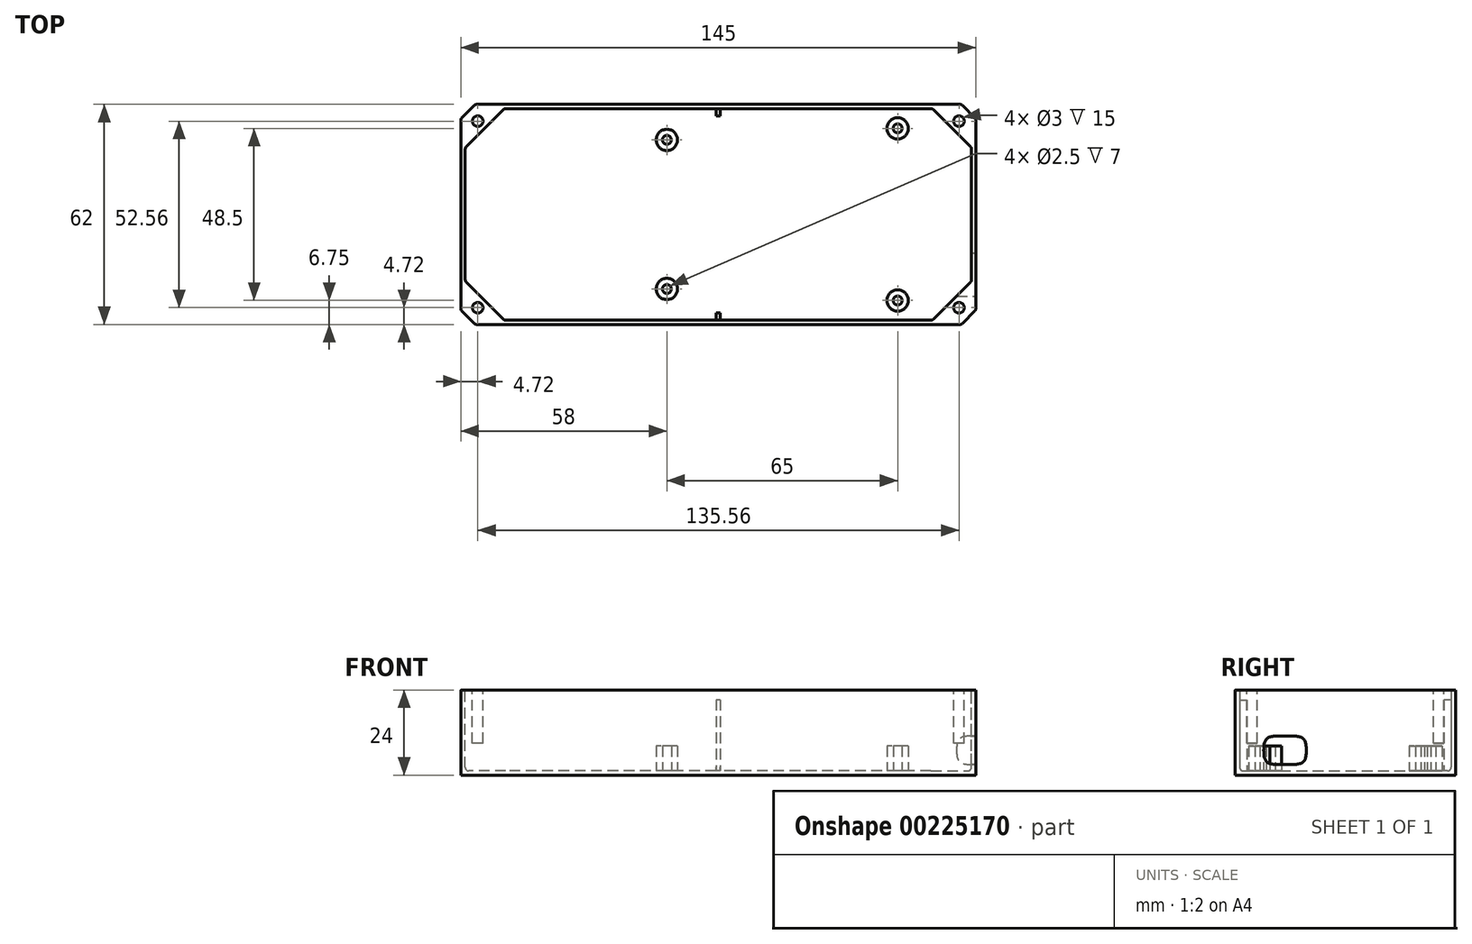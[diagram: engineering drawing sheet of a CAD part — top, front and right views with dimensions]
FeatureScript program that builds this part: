
annotation { "Feature Type Name" : "Feature", "Feature Type Description" : "" }
export const myFeature = defineFeature(function(context is Context, id is Id, definition is map)
    precondition{}
    {
        {
            var Q0;
            Q0=qCreatedBy(makeId("Top.planeOp"),FACE);
            var sketch = newSketch(context, id + "F0", { "sketchPlane" : qUnion([Q0])});
            skLineSegment(sketch, "E0.bottom", {"start": v(72.5, -31) * mm, "end": v(-72.5, -31) * mm});
            skLineSegment(sketch, "E0.top", {"start": v(72.5, 31) * mm, "end": v(-72.5, 31) * mm});
            skLineSegment(sketch, "E0.left", {"start": v(72.5, -31) * mm, "end": v(72.5, 31) * mm});
            skLineSegment(sketch, "E0.right", {"start": v(-72.5, -31) * mm, "end": v(-72.5, 31) * mm});
            skPoint(sketch, "E0.middle", {"position": v(0, 0) * mm});
            skSolve(sketch);
        }
        {
            var Q0;
            Q0=qSketchRegion(id+"F0",true);
            extrude(context, id + "F1", {"entities" : qUnion([Q0]), "depth" : 24 * mm});
        }
        {
            var Q0;
            Q0=makeQuery(id+"F1.opExtrude","CAP_FACE",FACE,{"disambiguationData":[OSD([sQuery(id+"F0.wireOp",EDGE,"E0.bottom"),sQuery(id+"F0.wireOp",EDGE,"E0.top"),sQuery(id+"F0.wireOp",EDGE,"E0.left"),sQuery(id+"F0.wireOp",EDGE,"E0.right")])],"isStart":false});
            var Q1;
            Q1=makeQuery(id+"F1.opExtrude","SWEPT_BODY",BODY,{"disambiguationData":[OSD([sQuery(id+"F0.wireOp",EDGE,"E0.bottom"),sQuery(id+"F0.wireOp",EDGE,"E0.top"),sQuery(id+"F0.wireOp",EDGE,"E0.left"),sQuery(id+"F0.wireOp",EDGE,"E0.right")])]});
            shell(context, id + "F2", {"entities" : qUnion([Q0]), "parts" : qUnion([Q1]), "thickness" : 1.2 * mm});
        }
        {
            var Q0;
            Q0=makeQuery(id+"F2.opShell","OFFSET_EDGE",EDGE,{"disambiguationData":[OSD([sQuery(id+"F0.wireOp",EDGE,"E0.top"),sQuery(id+"F0.wireOp",EDGE,"E0.left")])]});
            var Q1;
            Q1=makeQuery(id+"F2.opShell","OFFSET_EDGE",EDGE,{"disambiguationData":[OSD([sQuery(id+"F0.wireOp",EDGE,"E0.top"),sQuery(id+"F0.wireOp",EDGE,"E0.right")])]});
            var Q2;
            Q2=makeQuery(id+"F2.opShell","OFFSET_EDGE",EDGE,{"disambiguationData":[OSD([sQuery(id+"F0.wireOp",EDGE,"E0.bottom"),sQuery(id+"F0.wireOp",EDGE,"E0.right")])]});
            var Q3;
            Q3=makeQuery(id+"F2.opShell","OFFSET_EDGE",EDGE,{"disambiguationData":[OSD([sQuery(id+"F0.wireOp",EDGE,"E0.bottom"),sQuery(id+"F0.wireOp",EDGE,"E0.left")])]});
            chamfer(context, id + "F3", {"entities" : qUnion([Q0, Q1, Q2, Q3]), "width" : 11 * mm, "tangentPropagation" : true});
        }
        {
            var Q0;
            Q0=makeQuery(id+"F1.opExtrude","SWEPT_EDGE",EDGE,{"disambiguationData":[OSD([sQuery(id+"F0.wireOp",EDGE,"E0.bottom"),sQuery(id+"F0.wireOp",EDGE,"E0.right")])]});
            var Q1;
            Q1=makeQuery(id+"F1.opExtrude","SWEPT_EDGE",EDGE,{"disambiguationData":[OSD([sQuery(id+"F0.wireOp",EDGE,"E0.top"),sQuery(id+"F0.wireOp",EDGE,"E0.right")])]});
            var Q2;
            Q2=makeQuery(id+"F1.opExtrude","SWEPT_EDGE",EDGE,{"disambiguationData":[OSD([sQuery(id+"F0.wireOp",EDGE,"E0.bottom"),sQuery(id+"F0.wireOp",EDGE,"E0.left")])]});
            var Q3;
            Q3=makeQuery(id+"F1.opExtrude","SWEPT_EDGE",EDGE,{"disambiguationData":[OSD([sQuery(id+"F0.wireOp",EDGE,"E0.top"),sQuery(id+"F0.wireOp",EDGE,"E0.left")])]});
            chamfer(context, id + "F4", {"entities" : qUnion([Q0, Q1, Q2, Q3]), "width" : 4 * mm, "tangentPropagation" : true});
        }
        {
            var Q0;
            Q0=makeQuery(id+"F1.opExtrude","CAP_FACE",FACE,{"disambiguationData":[OSD([sQuery(id+"F0.wireOp",EDGE,"E0.bottom"),sQuery(id+"F0.wireOp",EDGE,"E0.top"),sQuery(id+"F0.wireOp",EDGE,"E0.left"),sQuery(id+"F0.wireOp",EDGE,"E0.right")])],"isStart":false});
            var sketch = newSketch(context, id + "F5", { "sketchPlane" : qUnion([Q0])});
            skCircle(sketch, "E1", {"center": v(-67.78, -26.28) * mm, "radius": 1.5 * mm});
            skCircle(sketch, "E2", {"center": v(-67.78, 26.28) * mm, "radius": 1.5 * mm});
            skCircle(sketch, "E3", {"center": v(67.78, 26.28) * mm, "radius": 1.5 * mm});
            skCircle(sketch, "E4", {"center": v(67.78, -26.28) * mm, "radius": 1.5 * mm});
            skLineSegment(sketch, "E5", {"start": v(-70.5, -29) * mm, "end": v(-65.8, -24.3) * mm, "construction": true});
            skLineSegment(sketch, "E6", {"start": v(-70.5, 29) * mm, "end": v(-65.8, 24.3) * mm, "construction": true});
            skLineSegment(sketch, "E7", {"start": v(70.5, 29) * mm, "end": v(65.8, 24.3) * mm, "construction": true});
            skLineSegment(sketch, "E8", {"start": v(70.5, -29) * mm, "end": v(65.8, -24.3) * mm, "construction": true});
            skSolve(sketch);
        }
        {
            var Q0;
            Q0=makeQuery(id+"F5.imprint","IMPRINT",FACE,{"disambiguationData":[TD([[makeQuery(id+"F5.imprint","IMPRINT",EDGE,{"derivedFrom":sQuery(id+"F5.wireOp",EDGE,"E2")}),1.0]])]});
            var Q1;
            Q1=makeQuery(id+"F5.imprint","IMPRINT",FACE,{"disambiguationData":[TD([[makeQuery(id+"F5.imprint","IMPRINT",EDGE,{"derivedFrom":sQuery(id+"F5.wireOp",EDGE,"E1")}),1.0]])]});
            var Q2;
            Q2=makeQuery(id+"F5.imprint","IMPRINT",FACE,{"disambiguationData":[TD([[makeQuery(id+"F5.imprint","IMPRINT",EDGE,{"derivedFrom":sQuery(id+"F5.wireOp",EDGE,"E4")}),1.0]])]});
            var Q3;
            Q3=makeQuery(id+"F5.imprint","IMPRINT",FACE,{"disambiguationData":[TD([[makeQuery(id+"F5.imprint","IMPRINT",EDGE,{"derivedFrom":sQuery(id+"F5.wireOp",EDGE,"E3")}),1.0]])]});
            extrude(context, id + "F6", {"entities" : qUnion([Q0, Q1, Q2, Q3]), "operationType" : NewBodyOperationType.REMOVE, "oppositeDirection" : true, "depth" : 15 * mm});
        }
        {
            var Q0;
            Q0=makeQuery(id+"F2.opShell","OFFSET_FACE",FACE,{"disambiguationData":[OSD([sQuery(id+"F0.wireOp",EDGE,"E0.bottom"),sQuery(id+"F0.wireOp",EDGE,"E0.top"),sQuery(id+"F0.wireOp",EDGE,"E0.left"),sQuery(id+"F0.wireOp",EDGE,"E0.right")])]});
            var sketch = newSketch(context, id + "F7", { "sketchPlane" : qUnion([Q0])});
            skCircle(sketch, "E9", {"center": v(50.5, 24.25) * mm, "radius": 3 * mm});
            skCircle(sketch, "E10.0.1.0", {"center": v(50.5, -24.25) * mm, "radius": 3 * mm});
            skCircle(sketch, "E10.1.0.0", {"center": v(-14.5, 21) * mm, "radius": 3 * mm});
            skCircle(sketch, "E10.1.1.0", {"center": v(-14.5, -21.01) * mm, "radius": 3 * mm});
            skCircle(sketch, "E11.0", {"center": v(-14.5, 21) * mm, "radius": 1.25 * mm});
            skCircle(sketch, "E12.0", {"center": v(50.5, 24.25) * mm, "radius": 1.25 * mm});
            skCircle(sketch, "E13.0", {"center": v(50.5, -24.25) * mm, "radius": 1.25 * mm});
            skCircle(sketch, "E14.0", {"center": v(-14.5, -21.01) * mm, "radius": 1.25 * mm});
            skLineSegment(sketch, "E15.bottom", {"start": v(0.57, -29.8) * mm, "end": v(-0.63, -29.8) * mm});
            skLineSegment(sketch, "E15.top", {"start": v(0.57, -27.8) * mm, "end": v(-0.63, -27.8) * mm});
            skLineSegment(sketch, "E15.left", {"start": v(0.57, -29.8) * mm, "end": v(0.57, -27.8) * mm});
            skLineSegment(sketch, "E15.right", {"start": v(-0.63, -29.8) * mm, "end": v(-0.63, -27.8) * mm});
            skLineSegment(sketch, "E16.bottom", {"start": v(-0.63, 29.8) * mm, "end": v(0.57, 29.8) * mm});
            skLineSegment(sketch, "E16.top", {"start": v(-0.63, 27.8) * mm, "end": v(0.57, 27.8) * mm});
            skLineSegment(sketch, "E16.left", {"start": v(-0.63, 29.8) * mm, "end": v(-0.63, 27.8) * mm});
            skLineSegment(sketch, "E16.right", {"start": v(0.57, 29.8) * mm, "end": v(0.57, 27.8) * mm});
            skSolve(sketch);
        }
        {
            var Q0;
            Q0=makeQuery(id+"F7.imprint","IMPRINT",FACE,{"disambiguationData":[TD([[makeQuery(id+"F7.imprint","IMPRINT",EDGE,{"derivedFrom":sQuery(id+"F7.wireOp",EDGE,"E10.1.1.0")}),1.0]])]});
            var Q1;
            Q1=makeQuery(id+"F7.imprint","IMPRINT",FACE,{"disambiguationData":[TD([[makeQuery(id+"F7.imprint","IMPRINT",EDGE,{"derivedFrom":sQuery(id+"F7.wireOp",EDGE,"E10.0.1.0")}),1.0]])]});
            var Q2;
            Q2=makeQuery(id+"F7.imprint","IMPRINT",FACE,{"disambiguationData":[TD([[makeQuery(id+"F7.imprint","IMPRINT",EDGE,{"derivedFrom":sQuery(id+"F7.wireOp",EDGE,"E9")}),1.0]])]});
            var Q3;
            Q3=makeQuery(id+"F7.imprint","IMPRINT",FACE,{"disambiguationData":[TD([[makeQuery(id+"F7.imprint","IMPRINT",EDGE,{"derivedFrom":sQuery(id+"F7.wireOp",EDGE,"E10.1.0.0")}),1.0]])]});
            var Q4;
            Q4=makeQuery(id+"F7.imprint","IMPRINT",FACE,{"disambiguationData":[TD([[makeQuery(id+"F7.imprint","IMPRINT",EDGE,{"derivedFrom":sQuery(id+"F7.wireOp",EDGE,"QgqdjcWb-DzXd-Z8pY-Gpl7-SXe3pRGrYA3b")}),1.0]])]});
            var Q5;
            Q5=makeQuery(id+"F7.imprint","IMPRINT",FACE,{"disambiguationData":[TD([[makeQuery(id+"F7.imprint","IMPRINT",EDGE,{"derivedFrom":sQuery(id+"F7.wireOp",EDGE,"DI5szFfg-u1AR-weB2-Kjsq-C97WaRRW3o7K")}),1.0]])]});
            extrude(context, id + "F8", {"entities" : qUnion([Q0, Q1, Q2, Q3, Q4, Q5]), "operationType" : NewBodyOperationType.ADD, "depth" : 7 * mm});
        }
        {
            var Q0;
            Q0=makeQuery(id+"F7.imprint","IMPRINT",FACE,{"disambiguationData":[TD([[makeQuery(id+"F7.imprint","IMPRINT",EDGE,{"derivedFrom":sQuery(id+"F7.wireOp",EDGE,"E16.bottom")}),1.0]])]});
            var Q1;
            Q1=makeQuery(id+"F7.imprint","IMPRINT",FACE,{"disambiguationData":[TD([[makeQuery(id+"F7.imprint","IMPRINT",EDGE,{"derivedFrom":sQuery(id+"F7.wireOp",EDGE,"E15.bottom")}),-1.0]])]});
            extrude(context, id + "F9", {"entities" : qUnion([Q0, Q1]), "operationType" : NewBodyOperationType.ADD, "depth" : 20 * mm});
        }
        {
            var Q0;
            Q0=makeQuery(id+"F1.opExtrude","SWEPT_FACE",FACE,{"disambiguationData":[OSD([sQuery(id+"F0.wireOp",EDGE,"E0.left")])]});
            var sketch = newSketch(context, id + "F10", { "sketchPlane" : qUnion([Q0])});
            skLineSegment(sketch, "E17.bottom", {"start": v(-23, 3) * mm, "end": v(-11, 3) * mm});
            skLineSegment(sketch, "E17.top", {"start": v(-23, 11) * mm, "end": v(-11, 11) * mm});
            skLineSegment(sketch, "E17.left", {"start": v(-23, 3) * mm, "end": v(-23, 11) * mm});
            skLineSegment(sketch, "E17.right", {"start": v(-11, 3) * mm, "end": v(-11, 11) * mm});
            skSolve(sketch);
        }
        {
            var Q0;
            Q0=makeQuery(id+"F10.imprint","IMPRINT",FACE,{"disambiguationData":[TD([[makeQuery(id+"F10.imprint","IMPRINT",EDGE,{"derivedFrom":sQuery(id+"F10.wireOp",EDGE,"E17.bottom")}),1.0]])]});
            extrude(context, id + "F11", {"entities" : qUnion([Q0]), "operationType" : NewBodyOperationType.REMOVE, "endBound" : BoundingType.UP_TO_NEXT, "oppositeDirection" : true, "depth" : 25 * mm});
        }
        {
            var Q0;
            Q0=makeQuery(id+"F11.boolean.opBoolean","COPY",EDGE,{"derivedFrom":makeQuery(id+"F11.opExtrude","SWEPT_EDGE",EDGE,{"disambiguationData":[OSD([sQuery(id+"F10.wireOp",EDGE,"E17.bottom"),sQuery(id+"F10.wireOp",EDGE,"E17.right")])]})});
            var Q1;
            Q1=makeQuery(id+"F11.boolean.opBoolean","COPY",EDGE,{"derivedFrom":makeQuery(id+"F11.opExtrude","SWEPT_EDGE",EDGE,{"disambiguationData":[OSD([sQuery(id+"F10.wireOp",EDGE,"E17.top"),sQuery(id+"F10.wireOp",EDGE,"E17.right")])]})});
            var Q2;
            Q2=makeQuery(id+"F11.boolean.opBoolean","COPY",EDGE,{"derivedFrom":makeQuery(id+"F11.opExtrude","SWEPT_EDGE",EDGE,{"disambiguationData":[OSD([sQuery(id+"F10.wireOp",EDGE,"E17.bottom"),sQuery(id+"F10.wireOp",EDGE,"E17.left")])]})});
            var Q3;
            Q3=makeQuery(id+"F11.boolean.opBoolean","COPY",EDGE,{"derivedFrom":makeQuery(id+"F11.opExtrude","SWEPT_EDGE",EDGE,{"disambiguationData":[OSD([sQuery(id+"F10.wireOp",EDGE,"E17.top"),sQuery(id+"F10.wireOp",EDGE,"E17.left")])]})});
            fillet(context, id + "F12", {"entities" : qUnion([Q0, Q1, Q2, Q3]), "radius" : 4 * mm, "tangentPropagation" : true, "rho" : 0.6, "crossSection" : FilletCrossSection.CONIC, "allowEdgeOverflow" : false});
        }
        {
            var Q0;
            {var subQ0=sQuery(id+"F0.wireOp",EDGE,"E0.top");Q0=makeQuery(id+"F3.opChamfer","BLEND_EDGE",EDGE,{"blendedFrom":[makeQuery(id+"F2.opShell","OFFSET_EDGE",EDGE,{"disambiguationData":[OSD([subQ0,sQuery(id+"F0.wireOp",EDGE,"E0.right")])]}),makeQuery(id+"F2.opShell","OFFSET_FACE",FACE,{"disambiguationData":[OSD([subQ0])]})],"blendedInto":[makeQuery(id+"F2.opShell","OFFSET_FACE",FACE,{"disambiguationData":[OSD([subQ0])]})]});}
            var Q1;
            {var subQ0=sQuery(id+"F0.wireOp",EDGE,"E0.right");Q1=makeQuery(id+"F3.opChamfer","BLEND_EDGE",EDGE,{"blendedFrom":[makeQuery(id+"F2.opShell","OFFSET_EDGE",EDGE,{"disambiguationData":[OSD([sQuery(id+"F0.wireOp",EDGE,"E0.top"),subQ0])]}),makeQuery(id+"F2.opShell","OFFSET_FACE",FACE,{"disambiguationData":[OSD([subQ0])]})],"blendedInto":[makeQuery(id+"F2.opShell","OFFSET_FACE",FACE,{"disambiguationData":[OSD([subQ0])]})]});}
            var Q2;
            {var subQ0=sQuery(id+"F0.wireOp",EDGE,"E0.top");Q2=makeQuery(id+"F3.opChamfer","BLEND_EDGE",EDGE,{"blendedFrom":[makeQuery(id+"F2.opShell","OFFSET_EDGE",EDGE,{"disambiguationData":[OSD([subQ0,sQuery(id+"F0.wireOp",EDGE,"E0.left")])]}),makeQuery(id+"F2.opShell","OFFSET_FACE",FACE,{"disambiguationData":[OSD([subQ0])]})],"blendedInto":[makeQuery(id+"F2.opShell","OFFSET_FACE",FACE,{"disambiguationData":[OSD([subQ0])]})]});}
            var Q3;
            {var subQ0=sQuery(id+"F0.wireOp",EDGE,"E0.left");Q3=makeQuery(id+"F3.opChamfer","BLEND_EDGE",EDGE,{"blendedFrom":[makeQuery(id+"F2.opShell","OFFSET_EDGE",EDGE,{"disambiguationData":[OSD([sQuery(id+"F0.wireOp",EDGE,"E0.top"),subQ0])]}),makeQuery(id+"F2.opShell","OFFSET_FACE",FACE,{"disambiguationData":[OSD([subQ0])]})],"blendedInto":[makeQuery(id+"F2.opShell","OFFSET_FACE",FACE,{"disambiguationData":[OSD([subQ0])]})]});}
            var Q4;
            {var subQ0=sQuery(id+"F0.wireOp",EDGE,"E0.bottom");Q4=makeQuery(id+"F3.opChamfer","BLEND_EDGE",EDGE,{"blendedFrom":[makeQuery(id+"F2.opShell","OFFSET_EDGE",EDGE,{"disambiguationData":[OSD([subQ0,sQuery(id+"F0.wireOp",EDGE,"E0.left")])]}),makeQuery(id+"F2.opShell","OFFSET_FACE",FACE,{"disambiguationData":[OSD([subQ0])]})],"blendedInto":[makeQuery(id+"F2.opShell","OFFSET_FACE",FACE,{"disambiguationData":[OSD([subQ0])]})]});}
            var Q5;
            {var subQ0=sQuery(id+"F0.wireOp",EDGE,"E0.bottom");Q5=makeQuery(id+"F3.opChamfer","BLEND_EDGE",EDGE,{"blendedFrom":[makeQuery(id+"F2.opShell","OFFSET_EDGE",EDGE,{"disambiguationData":[OSD([subQ0,sQuery(id+"F0.wireOp",EDGE,"E0.right")])]}),makeQuery(id+"F2.opShell","OFFSET_FACE",FACE,{"disambiguationData":[OSD([subQ0])]})],"blendedInto":[makeQuery(id+"F2.opShell","OFFSET_FACE",FACE,{"disambiguationData":[OSD([subQ0])]})]});}
            var Q6;
            {var subQ0=sQuery(id+"F0.wireOp",EDGE,"E0.right");Q6=makeQuery(id+"F3.opChamfer","BLEND_EDGE",EDGE,{"blendedFrom":[makeQuery(id+"F2.opShell","OFFSET_EDGE",EDGE,{"disambiguationData":[OSD([sQuery(id+"F0.wireOp",EDGE,"E0.bottom"),subQ0])]}),makeQuery(id+"F2.opShell","OFFSET_FACE",FACE,{"disambiguationData":[OSD([subQ0])]})],"blendedInto":[makeQuery(id+"F2.opShell","OFFSET_FACE",FACE,{"disambiguationData":[OSD([subQ0])]})]});}
            var Q7;
            {var subQ0=sQuery(id+"F0.wireOp",EDGE,"E0.right");Q7=makeQuery(id+"F4.opChamfer","BLEND_EDGE",EDGE,{"blendedFrom":[makeQuery(id+"F1.opExtrude","SWEPT_EDGE",EDGE,{"disambiguationData":[OSD([sQuery(id+"F0.wireOp",EDGE,"E0.bottom"),subQ0])]}),makeQuery(id+"F1.opExtrude","SWEPT_FACE",FACE,{"disambiguationData":[OSD([subQ0])]})],"blendedInto":[makeQuery(id+"F1.opExtrude","SWEPT_FACE",FACE,{"disambiguationData":[OSD([subQ0])]})]});}
            var Q8;
            {var subQ0=sQuery(id+"F0.wireOp",EDGE,"E0.bottom");Q8=makeQuery(id+"F4.opChamfer","BLEND_EDGE",EDGE,{"blendedFrom":[makeQuery(id+"F1.opExtrude","SWEPT_EDGE",EDGE,{"disambiguationData":[OSD([subQ0,sQuery(id+"F0.wireOp",EDGE,"E0.right")])]}),makeQuery(id+"F1.opExtrude","SWEPT_FACE",FACE,{"disambiguationData":[OSD([subQ0])]})],"blendedInto":[makeQuery(id+"F1.opExtrude","SWEPT_FACE",FACE,{"disambiguationData":[OSD([subQ0])]})]});}
            var Q9;
            {var subQ0=sQuery(id+"F0.wireOp",EDGE,"E0.bottom");Q9=makeQuery(id+"F4.opChamfer","BLEND_EDGE",EDGE,{"blendedFrom":[makeQuery(id+"F1.opExtrude","SWEPT_EDGE",EDGE,{"disambiguationData":[OSD([subQ0,sQuery(id+"F0.wireOp",EDGE,"E0.left")])]}),makeQuery(id+"F1.opExtrude","SWEPT_FACE",FACE,{"disambiguationData":[OSD([subQ0])]})],"blendedInto":[makeQuery(id+"F1.opExtrude","SWEPT_FACE",FACE,{"disambiguationData":[OSD([subQ0])]})]});}
            var Q10;
            {var subQ0=sQuery(id+"F0.wireOp",EDGE,"E0.left");Q10=makeQuery(id+"F4.opChamfer","BLEND_EDGE",EDGE,{"blendedFrom":[makeQuery(id+"F1.opExtrude","SWEPT_EDGE",EDGE,{"disambiguationData":[OSD([sQuery(id+"F0.wireOp",EDGE,"E0.bottom"),subQ0])]}),makeQuery(id+"F1.opExtrude","SWEPT_FACE",FACE,{"disambiguationData":[OSD([subQ0])]})],"blendedInto":[makeQuery(id+"F1.opExtrude","SWEPT_FACE",FACE,{"disambiguationData":[OSD([subQ0])]})]});}
            var Q11;
            {var subQ0=sQuery(id+"F0.wireOp",EDGE,"E0.left");Q11=makeQuery(id+"F4.opChamfer","BLEND_EDGE",EDGE,{"blendedFrom":[makeQuery(id+"F1.opExtrude","SWEPT_EDGE",EDGE,{"disambiguationData":[OSD([sQuery(id+"F0.wireOp",EDGE,"E0.top"),subQ0])]}),makeQuery(id+"F1.opExtrude","SWEPT_FACE",FACE,{"disambiguationData":[OSD([subQ0])]})],"blendedInto":[makeQuery(id+"F1.opExtrude","SWEPT_FACE",FACE,{"disambiguationData":[OSD([subQ0])]})]});}
            var Q12;
            {var subQ0=sQuery(id+"F0.wireOp",EDGE,"E0.top");Q12=makeQuery(id+"F4.opChamfer","BLEND_EDGE",EDGE,{"blendedFrom":[makeQuery(id+"F1.opExtrude","SWEPT_EDGE",EDGE,{"disambiguationData":[OSD([subQ0,sQuery(id+"F0.wireOp",EDGE,"E0.left")])]}),makeQuery(id+"F1.opExtrude","SWEPT_FACE",FACE,{"disambiguationData":[OSD([subQ0])]})],"blendedInto":[makeQuery(id+"F1.opExtrude","SWEPT_FACE",FACE,{"disambiguationData":[OSD([subQ0])]})]});}
            var Q13;
            {var subQ0=sQuery(id+"F0.wireOp",EDGE,"E0.top");Q13=makeQuery(id+"F4.opChamfer","BLEND_EDGE",EDGE,{"blendedFrom":[makeQuery(id+"F1.opExtrude","SWEPT_EDGE",EDGE,{"disambiguationData":[OSD([subQ0,sQuery(id+"F0.wireOp",EDGE,"E0.right")])]}),makeQuery(id+"F1.opExtrude","SWEPT_FACE",FACE,{"disambiguationData":[OSD([subQ0])]})],"blendedInto":[makeQuery(id+"F1.opExtrude","SWEPT_FACE",FACE,{"disambiguationData":[OSD([subQ0])]})]});}
            var Q14;
            {var subQ0=sQuery(id+"F0.wireOp",EDGE,"E0.right");Q14=makeQuery(id+"F4.opChamfer","BLEND_EDGE",EDGE,{"blendedFrom":[makeQuery(id+"F1.opExtrude","SWEPT_EDGE",EDGE,{"disambiguationData":[OSD([sQuery(id+"F0.wireOp",EDGE,"E0.top"),subQ0])]}),makeQuery(id+"F1.opExtrude","SWEPT_FACE",FACE,{"disambiguationData":[OSD([subQ0])]})],"blendedInto":[makeQuery(id+"F1.opExtrude","SWEPT_FACE",FACE,{"disambiguationData":[OSD([subQ0])]})]});}
            var Q15;
            {var subQ0=sQuery(id+"F0.wireOp",EDGE,"E0.left");Q15=makeQuery(id+"F3.opChamfer","BLEND_EDGE",EDGE,{"blendedFrom":[makeQuery(id+"F2.opShell","OFFSET_EDGE",EDGE,{"disambiguationData":[OSD([sQuery(id+"F0.wireOp",EDGE,"E0.bottom"),subQ0])]}),makeQuery(id+"F2.opShell","OFFSET_FACE",FACE,{"disambiguationData":[OSD([subQ0])]})],"blendedInto":[makeQuery(id+"F2.opShell","OFFSET_FACE",FACE,{"disambiguationData":[OSD([subQ0])]})]});}
            var Q16;
            {var subQ0=sQuery(id+"F0.wireOp",EDGE,"E0.left");Q16=makeQuery(id+"F2.opShell","OFFSET_EDGE",EDGE,{"disambiguationData":[OSD([subQ0]),TDD([makeQuery(id+"F1.opExtrude","CAP_EDGE",EDGE,{"disambiguationData":[OSD([subQ0])],"isStart":true})])]});}
            var Q17;
            {var subQ0=sQuery(id+"F0.wireOp",EDGE,"E0.left");var subQ1=sQuery(id+"F0.wireOp",EDGE,"E0.top");Q17=makeQuery(id+"F3.opChamfer","BLEND_EDGE",EDGE,{"blendedFrom":[makeQuery(id+"F2.opShell","OFFSET_EDGE",EDGE,{"disambiguationData":[OSD([subQ1,subQ0])]}),makeQuery(id+"F2.opShell","OFFSET_FACE",FACE,{"disambiguationData":[OSD([sQuery(id+"F0.wireOp",EDGE,"E0.bottom"),subQ1,subQ0,sQuery(id+"F0.wireOp",EDGE,"E0.right")])]})],"blendedInto":[makeQuery(id+"F2.opShell","OFFSET_FACE",FACE,{"disambiguationData":[OSD([sQuery(id+"F0.wireOp",EDGE,"E0.bottom"),subQ1,subQ0,sQuery(id+"F0.wireOp",EDGE,"E0.right")])]})]});}
            var Q18;
            {var subQ0=sQuery(id+"F0.wireOp",EDGE,"E0.top");Q18=makeQuery(id+"F2.opShell","OFFSET_EDGE",EDGE,{"disambiguationData":[OSD([subQ0]),TDD([makeQuery(id+"F1.opExtrude","CAP_EDGE",EDGE,{"disambiguationData":[OSD([subQ0])],"isStart":true})])]});}
            var Q19;
            {var subQ0=sQuery(id+"F0.wireOp",EDGE,"E0.right");var subQ1=sQuery(id+"F0.wireOp",EDGE,"E0.top");Q19=makeQuery(id+"F3.opChamfer","BLEND_EDGE",EDGE,{"blendedFrom":[makeQuery(id+"F2.opShell","OFFSET_EDGE",EDGE,{"disambiguationData":[OSD([subQ1,subQ0])]}),makeQuery(id+"F2.opShell","OFFSET_FACE",FACE,{"disambiguationData":[OSD([sQuery(id+"F0.wireOp",EDGE,"E0.bottom"),subQ1,sQuery(id+"F0.wireOp",EDGE,"E0.left"),subQ0])]})],"blendedInto":[makeQuery(id+"F2.opShell","OFFSET_FACE",FACE,{"disambiguationData":[OSD([sQuery(id+"F0.wireOp",EDGE,"E0.bottom"),subQ1,sQuery(id+"F0.wireOp",EDGE,"E0.left"),subQ0])]})]});}
            var Q20;
            {var subQ0=sQuery(id+"F0.wireOp",EDGE,"E0.right");Q20=makeQuery(id+"F2.opShell","OFFSET_EDGE",EDGE,{"disambiguationData":[OSD([subQ0]),TDD([makeQuery(id+"F1.opExtrude","CAP_EDGE",EDGE,{"disambiguationData":[OSD([subQ0])],"isStart":true})])]});}
            var Q21;
            Q21=makeQuery(id+"F8.opExtrude","CAP_EDGE",EDGE,{"disambiguationData":[OSD([sQuery(id+"F7.wireOp",EDGE,"QgqdjcWb-DzXd-Z8pY-Gpl7-SXe3pRGrYA3b")])],"isStart":true});
            var Q22;
            Q22=makeQuery(id+"F8.opExtrude","CAP_EDGE",EDGE,{"disambiguationData":[OSD([sQuery(id+"F7.wireOp",EDGE,"E10.1.0.0")])],"isStart":true});
            var Q23;
            Q23=makeQuery(id+"F8.opExtrude","CAP_EDGE",EDGE,{"disambiguationData":[OSD([sQuery(id+"F7.wireOp",EDGE,"E9")])],"isStart":true});
            var Q24;
            Q24=makeQuery(id+"F8.opExtrude","CAP_EDGE",EDGE,{"disambiguationData":[OSD([sQuery(id+"F7.wireOp",EDGE,"E10.1.1.0")])],"isStart":true});
            var Q25;
            Q25=makeQuery(id+"F8.opExtrude","CAP_EDGE",EDGE,{"disambiguationData":[OSD([sQuery(id+"F7.wireOp",EDGE,"DI5szFfg-u1AR-weB2-Kjsq-C97WaRRW3o7K")])],"isStart":true});
            var Q26;
            {var subQ0=sQuery(id+"F0.wireOp",EDGE,"E0.right");var subQ1=sQuery(id+"F0.wireOp",EDGE,"E0.bottom");Q26=makeQuery(id+"F3.opChamfer","BLEND_EDGE",EDGE,{"blendedFrom":[makeQuery(id+"F2.opShell","OFFSET_EDGE",EDGE,{"disambiguationData":[OSD([subQ1,subQ0])]}),makeQuery(id+"F2.opShell","OFFSET_FACE",FACE,{"disambiguationData":[OSD([subQ1,sQuery(id+"F0.wireOp",EDGE,"E0.top"),sQuery(id+"F0.wireOp",EDGE,"E0.left"),subQ0])]})],"blendedInto":[makeQuery(id+"F2.opShell","OFFSET_FACE",FACE,{"disambiguationData":[OSD([subQ1,sQuery(id+"F0.wireOp",EDGE,"E0.top"),sQuery(id+"F0.wireOp",EDGE,"E0.left"),subQ0])]})]});}
            var Q27;
            {var subQ0=sQuery(id+"F0.wireOp",EDGE,"E0.bottom");Q27=makeQuery(id+"F2.opShell","OFFSET_EDGE",EDGE,{"disambiguationData":[OSD([subQ0]),TDD([makeQuery(id+"F1.opExtrude","CAP_EDGE",EDGE,{"disambiguationData":[OSD([subQ0])],"isStart":true})])]});}
            var Q28;
            Q28=makeQuery(id+"F8.opExtrude","CAP_EDGE",EDGE,{"disambiguationData":[OSD([sQuery(id+"F7.wireOp",EDGE,"E10.0.1.0")])],"isStart":true});
            var Q29;
            {var subQ0=sQuery(id+"F0.wireOp",EDGE,"E0.left");var subQ1=sQuery(id+"F0.wireOp",EDGE,"E0.bottom");Q29=makeQuery(id+"F3.opChamfer","BLEND_EDGE",EDGE,{"blendedFrom":[makeQuery(id+"F2.opShell","OFFSET_EDGE",EDGE,{"disambiguationData":[OSD([subQ1,subQ0])]}),makeQuery(id+"F2.opShell","OFFSET_FACE",FACE,{"disambiguationData":[OSD([subQ1,sQuery(id+"F0.wireOp",EDGE,"E0.top"),subQ0,sQuery(id+"F0.wireOp",EDGE,"E0.right")])]})],"blendedInto":[makeQuery(id+"F2.opShell","OFFSET_FACE",FACE,{"disambiguationData":[OSD([subQ1,sQuery(id+"F0.wireOp",EDGE,"E0.top"),subQ0,sQuery(id+"F0.wireOp",EDGE,"E0.right")])]})]});}
            var Q30;
            Q30=makeQuery(id+"F9.opExtrude","SWEPT_EDGE",EDGE,{"disambiguationData":[OSD([sQuery(id+"F0.wireOp",EDGE,"E0.bottom"),sQuery(id+"F7.wireOp",EDGE,"E15.bottom"),sQuery(id+"F7.wireOp",EDGE,"E15.right")])]});
            var Q31;
            Q31=makeQuery(id+"F9.opExtrude","SWEPT_EDGE",EDGE,{"disambiguationData":[OSD([sQuery(id+"F0.wireOp",EDGE,"E0.bottom"),sQuery(id+"F7.wireOp",EDGE,"E15.bottom"),sQuery(id+"F7.wireOp",EDGE,"E15.left")])]});
            var Q32;
            Q32=makeQuery(id+"F9.opExtrude","SWEPT_EDGE",EDGE,{"disambiguationData":[OSD([sQuery(id+"F0.wireOp",EDGE,"E0.top"),sQuery(id+"F7.wireOp",EDGE,"E16.bottom"),sQuery(id+"F7.wireOp",EDGE,"E16.right")])]});
            var Q33;
            Q33=makeQuery(id+"F9.opExtrude","SWEPT_EDGE",EDGE,{"disambiguationData":[OSD([sQuery(id+"F0.wireOp",EDGE,"E0.top"),sQuery(id+"F7.wireOp",EDGE,"E16.bottom"),sQuery(id+"F7.wireOp",EDGE,"E16.left")])]});
            var Q34;
            Q34=makeQuery(id+"F9.opExtrude","CAP_EDGE",EDGE,{"disambiguationData":[OSD([sQuery(id+"F7.wireOp",EDGE,"E16.left")])],"isStart":true});
            var Q35;
            Q35=makeQuery(id+"F9.opExtrude","CAP_EDGE",EDGE,{"disambiguationData":[OSD([sQuery(id+"F7.wireOp",EDGE,"E16.top")])],"isStart":true});
            var Q36;
            Q36=makeQuery(id+"F9.opExtrude","CAP_EDGE",EDGE,{"disambiguationData":[OSD([sQuery(id+"F7.wireOp",EDGE,"E16.right")])],"isStart":true});
            var Q37;
            Q37=makeQuery(id+"F9.opExtrude","CAP_EDGE",EDGE,{"disambiguationData":[OSD([sQuery(id+"F7.wireOp",EDGE,"E15.top")])],"isStart":true});
            var Q38;
            Q38=makeQuery(id+"F9.opExtrude","CAP_EDGE",EDGE,{"disambiguationData":[OSD([sQuery(id+"F7.wireOp",EDGE,"E15.right")])],"isStart":true});
            var Q39;
            Q39=makeQuery(id+"F9.opExtrude","CAP_EDGE",EDGE,{"disambiguationData":[OSD([sQuery(id+"F7.wireOp",EDGE,"E15.left")])],"isStart":true});
            fillet(context, id + "F13", {"entities" : qUnion([Q0, Q1, Q2, Q3, Q4, Q5, Q6, Q7, Q8, Q9, Q10, Q11, Q12, Q13, Q14, Q15, Q16, Q17, Q18, Q19, Q20, Q21, Q22, Q23, Q24, Q25, Q26, Q27, Q28, Q29, Q30, Q31, Q32, Q33, Q34, Q35, Q36, Q37, Q38, Q39]), "radius" : 1 * mm, "tangentPropagation" : true, "allowEdgeOverflow" : false});
        }
    });
